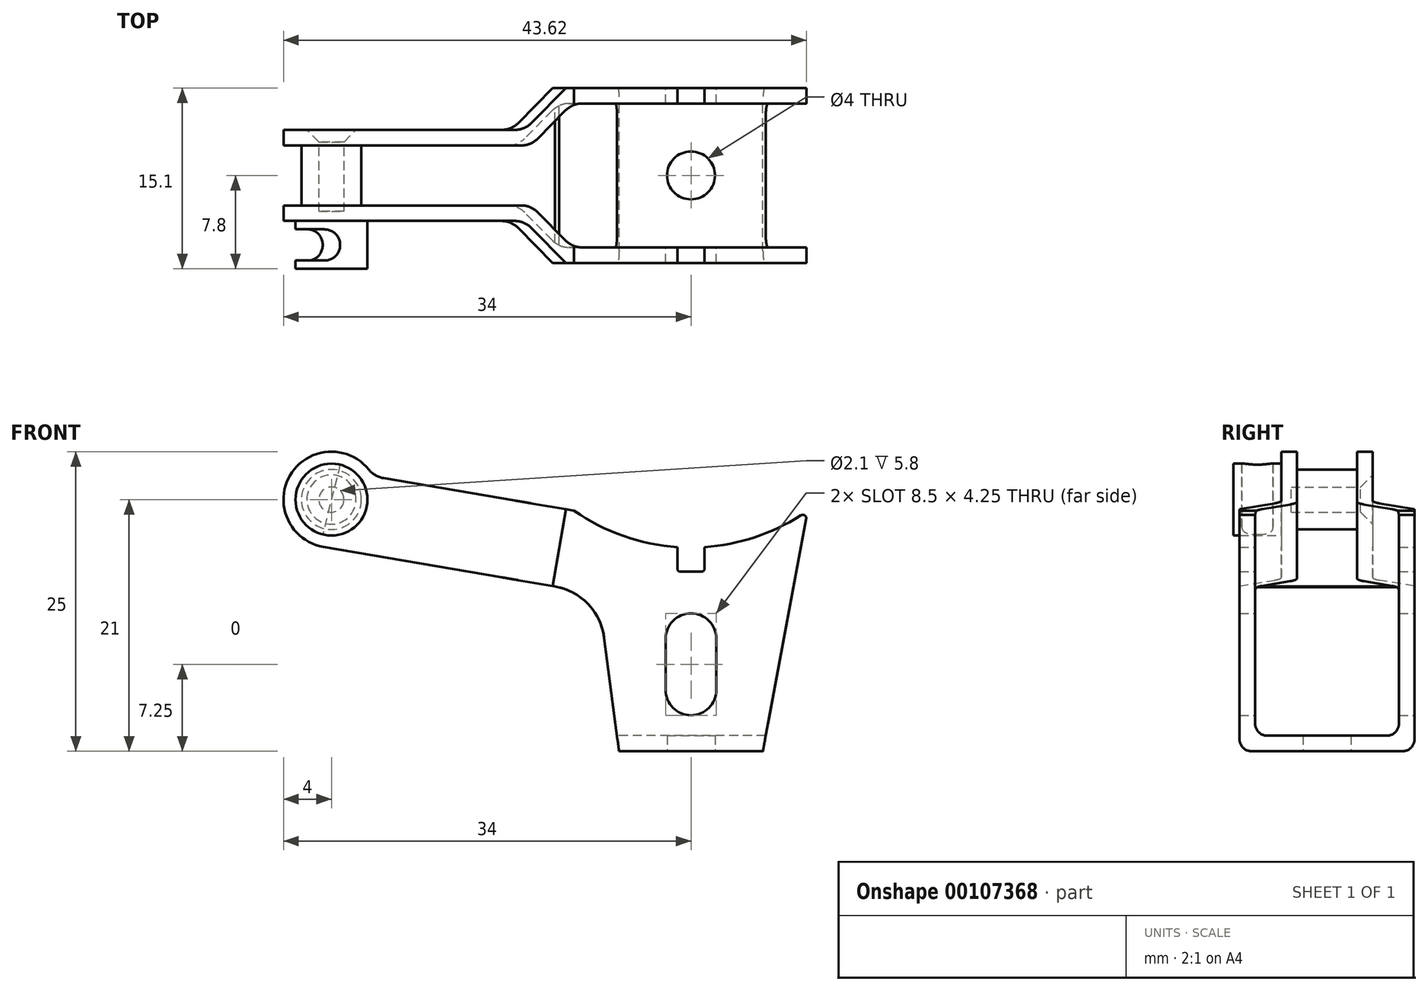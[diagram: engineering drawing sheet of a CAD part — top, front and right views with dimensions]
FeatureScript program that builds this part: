
annotation { "Feature Type Name" : "Feature", "Feature Type Description" : "" }
export const myFeature = defineFeature(function(context is Context, id is Id, definition is map)
    precondition{}
    {
        {
            var Q0;
            Q0=qCreatedBy(makeId("Front.planeOp"),FACE);
            var sketch = newSketch(context, id + "F0", { "sketchPlane" : qUnion([Q0])});
            skLineSegment(sketch, "E0", {"start": v(-6, 0) * mm, "end": v(6, 0) * mm});
            skLineSegment(sketch, "E1", {"start": v(6, 0) * mm, "end": v(9.62, 19.37) * mm});
            skLineSegment(sketch, "E2", {"start": v(-6, 0) * mm, "end": v(-7.25, 9.48) * mm});
            skArc(sketch, "E3", {"start": v(-9.75, 20.07) * mm, "mid": v(-0.35, 17) * mm, "end": v(9.16, 19.68) * mm});
            skLineSegment(sketch, "E4", {"start": v(0, 0) * mm, "end": v(0, 17) * mm, "construction": true});
            skLineSegment(sketch, "E5", {"start": v(-9.75, 20.07) * mm, "end": v(-25.67, 22.8) * mm});
            skArc(sketch, "E6", {"start": v(-26.89, 23.51) * mm, "mid": v(-33.45, 23.02) * mm, "end": v(-30.67, 17.06) * mm});
            skLineSegment(sketch, "E7", {"start": v(-30.67, 17.06) * mm, "end": v(-11.36, 13.76) * mm});
            skPoint(sketch, "E8.visualSharp", {"position": v(9.75, 20.07) * mm});
            skArc(sketch, "E8.filletArc", {"start": v(9.62, 19.37) * mm, "mid": v(9.5, 19.68) * mm, "end": v(9.16, 19.68) * mm});
            skPoint(sketch, "E9.visualSharp", {"position": v(-7.73, 13.13) * mm});
            skArc(sketch, "E9.filletArc", {"start": v(-7.25, 9.48) * mm, "mid": v(-8.6, 12.3) * mm, "end": v(-11.36, 13.76) * mm});
            skPoint(sketch, "E10.visualSharp", {"position": v(-26.5, 22.94) * mm});
            skArc(sketch, "E10.filletArc", {"start": v(-26.89, 23.51) * mm, "mid": v(-26.34, 23.04) * mm, "end": v(-25.67, 22.8) * mm});
            skLineSegment(sketch, "E11", {"start": v(9.75, 20.07) * mm, "end": v(0, 34) * mm});
            skLineSegment(sketch, "E12", {"start": v(-9.75, 20.07) * mm, "end": v(0, 34) * mm});
            skSolve(sketch);
        }
        {
            var Q0;
            Q0=makeQuery(id+"F0.imprint","IMPRINT",FACE,{"disambiguationData":[TD([[makeQuery(id+"F0.imprint","IMPRINT",EDGE,{"derivedFrom":sQuery(id+"F0.wireOp",EDGE,"E0")}),1.0]])]});
            extrude(context, id + "F1", {"entities" : qUnion([Q0]), "depth" : 7.3 * mm, "hasSecondDirection" : true, "secondDirectionOppositeDirection" : true, "secondDirectionDepth" : 7.3 * mm});
        }
        {
            var Q0;
            Q0=qCreatedBy(makeId("Front.planeOp"),FACE);
            var sketch = newSketch(context, id + "F2", { "sketchPlane" : qUnion([Q0])});
            skLineSegment(sketch, "E13", {"start": v(15, 78.04) * mm, "end": v(15, 1.3) * mm});
            skLineSegment(sketch, "E14", {"start": v(15, 1.3) * mm, "end": v(-11, 1.3) * mm});
            skLineSegment(sketch, "E15", {"start": v(0, 78.04) * mm, "end": v(15, 78.04) * mm});
            skLineSegment(sketch, "E16", {"start": v(-11, 1.3) * mm, "end": v(-11, 13.7) * mm});
            skLineSegment(sketch, "E17", {"start": v(-11, 13.7) * mm, "end": v(0, 78.04) * mm});
            skSolve(sketch);
        }
        {
            var Q0;
            Q0=makeQuery(id+"F2.imprint","IMPRINT",FACE,{"disambiguationData":[TD([[makeQuery(id+"F2.imprint","IMPRINT",EDGE,{"derivedFrom":sQuery(id+"F2.wireOp",EDGE,"E13")}),-1.0]])]});
            extrude(context, id + "F3", {"entities" : qUnion([Q0]), "operationType" : NewBodyOperationType.REMOVE, "depth" : 6 * mm, "hasSecondDirection" : true, "secondDirectionOppositeDirection" : true, "secondDirectionDepth" : 6 * mm});
        }
        {
            var Q0;
            Q0=qCreatedBy(makeId("Front.planeOp"),FACE);
            var sketch = newSketch(context, id + "F4", { "sketchPlane" : qUnion([Q0])});
            skLineSegment(sketch, "E18", {"start": v(-2.12, 9.38) * mm, "end": v(-2.12, 5.12) * mm});
            skArc(sketch, "E19", {"start": v(0, 11.5) * mm, "mid": v(-1.5, 10.88) * mm, "end": v(-2.13, 9.38) * mm});
            skArc(sketch, "E20", {"start": v(-2.12, 5.12) * mm, "mid": v(-1.5, 3.62) * mm, "end": v(0, 3) * mm});
            skArc(sketch, "E21.MirrorCS", {"start": v(0, 11.5) * mm, "mid": v(1.5, 10.88) * mm, "end": v(2.13, 9.38) * mm});
            skLineSegment(sketch, "E22.MirrorCS", {"start": v(2.12, 9.38) * mm, "end": v(2.12, 5.12) * mm});
            skArc(sketch, "E23.MirrorCS", {"start": v(2.12, 5.12) * mm, "mid": v(1.5, 3.62) * mm, "end": v(0, 3) * mm});
            skLineSegment(sketch, "E24", {"start": v(-1.12, 18) * mm, "end": v(-1.12, 15.2) * mm});
            skLineSegment(sketch, "E25", {"start": v(-0.92, 15) * mm, "end": v(0, 15) * mm});
            skLineSegment(sketch, "E26", {"start": v(0, 18) * mm, "end": v(-1.12, 18) * mm});
            skLineSegment(sketch, "E27.MirrorCS", {"start": v(0, 18) * mm, "end": v(1.12, 18) * mm});
            skLineSegment(sketch, "E28.MirrorCS", {"start": v(1.12, 18) * mm, "end": v(1.12, 15.2) * mm});
            skLineSegment(sketch, "E29.MirrorCS", {"start": v(0.93, 15) * mm, "end": v(0, 15) * mm});
            skPoint(sketch, "E30.visualSharp", {"position": v(-1.12, 15) * mm});
            skArc(sketch, "E30.filletArc", {"start": v(-1.12, 15.2) * mm, "mid": v(-1.07, 15.06) * mm, "end": v(-0.92, 15) * mm});
            skPoint(sketch, "E31.visualSharp", {"position": v(1.12, 15) * mm});
            skArc(sketch, "E31.filletArc", {"start": v(0.93, 15) * mm, "mid": v(1.07, 15.06) * mm, "end": v(1.12, 15.2) * mm});
            skSolve(sketch);
        }
        {
            var Q0;
            Q0=makeQuery(id+"F4.imprint","IMPRINT",FACE,{"disambiguationData":[TD([[makeQuery(id+"F4.imprint","IMPRINT",EDGE,{"derivedFrom":sQuery(id+"F4.wireOp",EDGE,"E24")}),1.0]])]});
            var Q1;
            Q1=makeQuery(id+"F4.imprint","IMPRINT",FACE,{"disambiguationData":[TD([[makeQuery(id+"F4.imprint","IMPRINT",EDGE,{"derivedFrom":sQuery(id+"F4.wireOp",EDGE,"E18")}),1.0]])]});
            extrude(context, id + "F5", {"entities" : qUnion([Q0, Q1]), "operationType" : NewBodyOperationType.REMOVE, "depth" : 10 * mm, "hasSecondDirection" : true, "secondDirectionOppositeDirection" : true, "secondDirectionDepth" : 10 * mm});
        }
        {
            var Q0;
            Q0=makeQuery(id+"F1.opExtrude","SWEPT_FACE",FACE,{"disambiguationData":[OSD([sQuery(id+"F0.wireOp",EDGE,"E7")])]});
            cPlane(context, id + "F6", {"entities" : qUnion([Q0]), "cplaneType" : CPlaneType.OFFSET, "offset" : 0 * mm, "width" : 150 * mm, "height" : 150 * mm});
        }
        {
            var Q0;
            Q0=qCreatedBy(id+"F6.planeOp",FACE);
            var sketch = newSketch(context, id + "F7", { "sketchPlane" : qUnion([Q0])});
            skLineSegment(sketch, "E32", {"start": v(-13.69, -7.3) * mm, "end": v(-17.19, -3.8) * mm});
            skLineSegment(sketch, "E33", {"start": v(-17.19, -3.8) * mm, "end": v(-42, -3.8) * mm});
            skLineSegment(sketch, "E34", {"start": v(-42, -3.8) * mm, "end": v(-42, -7.3) * mm});
            skLineSegment(sketch, "E35", {"start": v(-42, -7.3) * mm, "end": v(-13.69, -7.3) * mm});
            skLineSegment(sketch, "E36.MirrorCS", {"start": v(-42, 3.8) * mm, "end": v(-42, 7.3) * mm});
            skLineSegment(sketch, "E37.MirrorCS", {"start": v(-42, 7.3) * mm, "end": v(-13.69, 7.3) * mm});
            skLineSegment(sketch, "E38.MirrorCS", {"start": v(-13.69, 7.3) * mm, "end": v(-17.19, 3.8) * mm});
            skLineSegment(sketch, "E39.MirrorCS", {"start": v(-17.19, 3.8) * mm, "end": v(-42, 3.8) * mm});
            skLineSegment(sketch, "E40", {"start": v(-13.15, -6) * mm, "end": v(-16.65, -2.5) * mm});
            skLineSegment(sketch, "E41", {"start": v(-16.65, -2.5) * mm, "end": v(-42, -2.5) * mm});
            skLineSegment(sketch, "E42", {"start": v(-42, -2.5) * mm, "end": v(-42, 0) * mm});
            skLineSegment(sketch, "E43", {"start": v(-13.15, -6) * mm, "end": v(-13.15, 0) * mm});
            skLineSegment(sketch, "E44.MirrorCS", {"start": v(-13.15, 6) * mm, "end": v(-13.15, 0) * mm});
            skLineSegment(sketch, "E45.MirrorCS", {"start": v(-13.15, 6) * mm, "end": v(-16.65, 2.5) * mm});
            skLineSegment(sketch, "E46.MirrorCS", {"start": v(-16.65, 2.5) * mm, "end": v(-42, 2.5) * mm});
            skLineSegment(sketch, "E47.MirrorCS", {"start": v(-42, 2.5) * mm, "end": v(-42, 0) * mm});
            skSolve(sketch);
        }
        {
            var Q0;
            Q0=qSketchRegion(id+"F7",true);
            extrude(context, id + "F8", {"entities" : qUnion([Q0]), "operationType" : NewBodyOperationType.REMOVE, "oppositeDirection" : true, "depth" : 25 * mm});
        }
        {
            var Q0;
            Q0=qCreatedBy(makeId("Front.planeOp"),FACE);
            var sketch = newSketch(context, id + "F9", { "sketchPlane" : qUnion([Q0])});
            skCircle(sketch, "E48", {"center": v(-30, 21) * mm, "radius": 2.5 * mm});
            skSolve(sketch);
        }
        {
            var Q0;
            Q0=makeQuery(id+"F9.imprint","IMPRINT",FACE,{"disambiguationData":[TD([[makeQuery(id+"F9.imprint","IMPRINT",EDGE,{"derivedFrom":sQuery(id+"F9.wireOp",EDGE,"E48")}),1.0]])]});
            extrude(context, id + "F10", {"entities" : qUnion([Q0]), "operationType" : NewBodyOperationType.ADD, "endBound" : BoundingType.UP_TO_NEXT, "depth" : 10 * mm, "hasSecondDirection" : true, "secondDirectionBound" : SecondDirectionBoundingType.UP_TO_NEXT, "secondDirectionOppositeDirection" : true, "secondDirectionDepth" : 10 * mm});
        }
        {
            var Q0;
            Q0=makeQuery(id+"F8.boolean.opBoolean","COPY",EDGE,{"derivedFrom":makeQuery(id+"F8.opExtrude","SWEPT_EDGE",EDGE,{"disambiguationData":[OSD([sQuery(id+"F7.wireOp",EDGE,"E32"),sQuery(id+"F7.wireOp",EDGE,"E33")])]})});
            var Q1;
            Q1=makeQuery(id+"F8.boolean.opBoolean","COPY",EDGE,{"derivedFrom":makeQuery(id+"F8.opExtrude","SWEPT_EDGE",EDGE,{"disambiguationData":[OSD([sQuery(id+"F7.wireOp",EDGE,"E32"),sQuery(id+"F7.wireOp",EDGE,"E35")])]})});
            var Q2;
            Q2=makeQuery(id+"F8.boolean.opBoolean","COPY",EDGE,{"derivedFrom":makeQuery(id+"F8.opExtrude","SWEPT_EDGE",EDGE,{"disambiguationData":[OSD([sQuery(id+"F7.wireOp",EDGE,"E45.MirrorCS"),sQuery(id+"F7.wireOp",EDGE,"E46.MirrorCS")])]})});
            var Q3;
            Q3=makeQuery(id+"F8.boolean.opBoolean","MERGE",EDGE,{"derivedFrom":[makeQuery(id+"F3.boolean.opBoolean","COPY",EDGE,{"derivedFrom":makeQuery(id+"F3.opExtrude","CAP_EDGE",EDGE,{"disambiguationData":[OSD([sQuery(id+"F2.wireOp",EDGE,"E17")])],"isStart":false})}),makeQuery(id+"F8.opExtrude","SWEPT_EDGE",EDGE,{"disambiguationData":[OSD([sQuery(id+"F7.wireOp",EDGE,"E44.MirrorCS"),sQuery(id+"F7.wireOp",EDGE,"E45.MirrorCS")])]})]});
            var Q4;
            Q4=makeQuery(id+"F8.boolean.opBoolean","COPY",EDGE,{"derivedFrom":makeQuery(id+"F8.opExtrude","SWEPT_EDGE",EDGE,{"disambiguationData":[OSD([sQuery(id+"F7.wireOp",EDGE,"E37.MirrorCS"),sQuery(id+"F7.wireOp",EDGE,"E38.MirrorCS")])]})});
            var Q5;
            Q5=makeQuery(id+"F8.boolean.opBoolean","COPY",EDGE,{"derivedFrom":makeQuery(id+"F8.opExtrude","SWEPT_EDGE",EDGE,{"disambiguationData":[OSD([sQuery(id+"F7.wireOp",EDGE,"E38.MirrorCS"),sQuery(id+"F7.wireOp",EDGE,"E39.MirrorCS")])]})});
            var Q6;
            Q6=makeQuery(id+"F8.boolean.opBoolean","COPY",EDGE,{"derivedFrom":makeQuery(id+"F8.opExtrude","SWEPT_EDGE",EDGE,{"disambiguationData":[OSD([sQuery(id+"F7.wireOp",EDGE,"E40"),sQuery(id+"F7.wireOp",EDGE,"E41")])]})});
            var Q7;
            Q7=makeQuery(id+"F8.boolean.opBoolean","MERGE",EDGE,{"derivedFrom":[makeQuery(id+"F3.boolean.opBoolean","COPY",EDGE,{"derivedFrom":makeQuery(id+"F3.opExtrude","CAP_EDGE",EDGE,{"disambiguationData":[OSD([sQuery(id+"F2.wireOp",EDGE,"E17")])],"isStart":true})}),makeQuery(id+"F8.opExtrude","SWEPT_EDGE",EDGE,{"disambiguationData":[OSD([sQuery(id+"F7.wireOp",EDGE,"E40"),sQuery(id+"F7.wireOp",EDGE,"E43")])]})]});
            fillet(context, id + "F11", {"entities" : qUnion([Q0, Q1, Q2, Q3, Q4, Q5, Q6, Q7]), "radius" : 2 * mm, "tangentPropagation" : true, "allowEdgeOverflow" : false});
        }
        {
            var Q0;
            Q0=makeQuery(id+"F3.boolean.opBoolean","COPY",EDGE,{"derivedFrom":makeQuery(id+"F3.opExtrude","CAP_EDGE",EDGE,{"disambiguationData":[OSD([sQuery(id+"F2.wireOp",EDGE,"E14")])],"isStart":true})});
            var Q1;
            Q1=makeQuery(id+"F1.opExtrude","CAP_EDGE",EDGE,{"disambiguationData":[OSD([sQuery(id+"F0.wireOp",EDGE,"E0")])],"isStart":false});
            var Q2;
            Q2=makeQuery(id+"F3.boolean.opBoolean","COPY",EDGE,{"derivedFrom":makeQuery(id+"F3.opExtrude","CAP_EDGE",EDGE,{"disambiguationData":[OSD([sQuery(id+"F2.wireOp",EDGE,"E14")])],"isStart":false})});
            var Q3;
            Q3=makeQuery(id+"F1.opExtrude","CAP_EDGE",EDGE,{"disambiguationData":[OSD([sQuery(id+"F0.wireOp",EDGE,"E0")])],"isStart":true});
            fillet(context, id + "F12", {"entities" : qUnion([Q0, Q1, Q2, Q3]), "radius" : 1 * mm, "tangentPropagation" : true, "allowEdgeOverflow" : false});
        }
        {
            var Q0;
            Q0=qCreatedBy(makeId("Top.planeOp"),FACE);
            var sketch = newSketch(context, id + "F13", { "sketchPlane" : qUnion([Q0])});
            skCircle(sketch, "E49", {"center": v(0, 0) * mm, "radius": 2 * mm});
            skSolve(sketch);
        }
        {
            var Q0;
            Q0=qSketchRegion(id+"F13",true);
            extrude(context, id + "F14", {"entities" : qUnion([Q0]), "operationType" : NewBodyOperationType.REMOVE, "depth" : 5 * mm});
        }
        {
            var Q0;
            Q0=qCreatedBy(makeId("Front.planeOp"),FACE);
            var sketch = newSketch(context, id + "F15", { "sketchPlane" : qUnion([Q0])});
            skCircle(sketch, "E50", {"center": v(-30, 21) * mm, "radius": 1.05 * mm});
            skSolve(sketch);
        }
        {
            var Q0;
            Q0=makeQuery(id+"F15.imprint","IMPRINT",FACE,{"disambiguationData":[TD([[makeQuery(id+"F15.imprint","IMPRINT",EDGE,{"derivedFrom":sQuery(id+"F15.wireOp",EDGE,"E50")}),1.0]])]});
            extrude(context, id + "F16", {"entities" : qUnion([Q0]), "operationType" : NewBodyOperationType.REMOVE, "depth" : 3 * mm, "hasSecondDirection" : true, "secondDirectionOppositeDirection" : true, "secondDirectionDepth" : 10 * mm});
        }
        {
            var Q0;
            Q0=makeQuery(id+"F16.boolean.opBoolean","INTERSECT",EDGE,{"derivedFrom":[makeQuery(id+"F8.boolean.opBoolean","COPY",FACE,{"derivedFrom":makeQuery(id+"F8.opExtrude","SWEPT_FACE",FACE,{"disambiguationData":[OSD([sQuery(id+"F7.wireOp",EDGE,"E33")])]})}),makeQuery(id+"F16.opExtrude","SWEPT_FACE",FACE,{"disambiguationData":[OSD([sQuery(id+"F15.wireOp",EDGE,"E50")])]})]});
            chamfer(context, id + "F17", {"entities" : qUnion([Q0]), "width" : 1 * mm, "tangentPropagation" : true});
        }
        {
            var Q0;
            Q0=qCreatedBy(makeId("Front.planeOp"),FACE);
            var sketch = newSketch(context, id + "F18", { "sketchPlane" : qUnion([Q0])});
            skCircle(sketch, "E51", {"center": v(-30, 21) * mm, "radius": 3 * mm});
            skSolve(sketch);
        }
        {
            var Q0;
            Q0=makeQuery(id+"F18.imprint","IMPRINT",FACE,{"disambiguationData":[TD([[makeQuery(id+"F18.imprint","IMPRINT",EDGE,{"derivedFrom":sQuery(id+"F18.wireOp",EDGE,"E51")}),1.0]])]});
            extrude(context, id + "F19", {"entities" : qUnion([Q0]), "operationType" : NewBodyOperationType.ADD, "depth" : 7.8 * mm, "hasSecondDirection" : true, "secondDirectionOppositeDirection" : false, "secondDirectionDepth" : 3.8 * mm});
        }
        {
            var Q0;
            Q0=qCreatedBy(makeId("Front.planeOp"),FACE);
            var sketch = newSketch(context, id + "F20", { "sketchPlane" : qUnion([Q0])});
            skLineSegment(sketch, "E52", {"start": v(-31.81, 13.72) * mm, "end": v(-28.19, 28.28) * mm});
            skLineSegment(sketch, "E53", {"start": v(-28.19, 28.28) * mm, "end": v(-36.92, 30.45) * mm});
            skLineSegment(sketch, "E54", {"start": v(-36.92, 30.45) * mm, "end": v(-40.55, 15.9) * mm});
            skLineSegment(sketch, "E55", {"start": v(-40.55, 15.9) * mm, "end": v(-31.81, 13.72) * mm});
            skLineSegment(sketch, "E56", {"start": v(-38.73, 23.18) * mm, "end": v(-30, 21) * mm, "construction": true});
            skSolve(sketch);
        }
        {
            var Q0;
            Q0=makeQuery(id+"F20.imprint","IMPRINT",FACE,{"disambiguationData":[TD([[makeQuery(id+"F20.imprint","IMPRINT",EDGE,{"derivedFrom":sQuery(id+"F20.wireOp",EDGE,"E52")}),1.0]])]});
            extrude(context, id + "F21", {"entities" : qUnion([Q0]), "operationType" : NewBodyOperationType.REMOVE, "depth" : 7.1 * mm, "hasSecondDirection" : true, "secondDirectionOppositeDirection" : false, "secondDirectionDepth" : 4.5 * mm});
        }
        {
            var Q0;
            Q0=makeQuery(id+"F21.boolean.opBoolean","COPY",EDGE,{"derivedFrom":makeQuery(id+"F21.opExtrude","CAP_EDGE",EDGE,{"disambiguationData":[OSD([sQuery(id+"F20.wireOp",EDGE,"E52")])],"isStart":true})});
            var Q1;
            Q1=makeQuery(id+"F21.boolean.opBoolean","COPY",EDGE,{"derivedFrom":makeQuery(id+"F21.opExtrude","CAP_EDGE",EDGE,{"disambiguationData":[OSD([sQuery(id+"F20.wireOp",EDGE,"E52")])],"isStart":false})});
            fillet(context, id + "F22", {"entities" : qUnion([Q0, Q1]), "radius" : 1.3 * mm, "tangentPropagation" : true, "allowEdgeOverflow" : false});
        }
    });
